# Revit family: Magnuson-Valuta-Planter+
name_source: partatom
category: Furniture
units: mm (PartAtom-declared; Revit-internal decimal feet)

## family parameters
Always vertical = Yes
Cut with Voids When Loaded = No
Room Calculation Point = No
Shared = No
Work Plane-Based = No

## types (4) — shared parameters
Assembly Code = E2020200
Base Finish = MAG - Anodized Silver
Body Finish = MAG - Anodized Silver
Default Elevation = 0"
Depth = 17 7/8"
Glide Finish = MAG - Plastic Black
Keynote = 12500
Liner Finish = MAG - Plastic Black
Manufacturer = Magnuson Group
Product Documentation Link = https://magnusongroup.com
Revit File Built By = https://servex-us.com
Soil Finish = MAG - soil
Top Finish = MAG - Anodized Silver
Type Comments = Planters
URL = www.magnusongroup.com
zero-valued in all types: Cost

## per-type parameters (varying)
| type | Description | Height | Liner Height | Opening Depth | Opening Width | Width |
| VA1809L-JR-P | Indoor junior height painted steel rectangular planter with internal rigid liner and adjustable glides. | 26 1/8" | 6" | 13 19/32" | 4 19/32" | 8 7/8" |
| VA1818L-P | Indoor painted steel square planter with internal rigid liner and adjustable glides. | 34 7/32" | 12" | 12" | 12" | 17 7/8" |
| VA1814L-P | Indoor painted steel rectangular planter with internal rigid liner and adjustable glides. | 34 7/32" | 8" | 12" | 8" | 13 7/8" |
| VA1809L-P | Indoor painted steel rectangular planter with internal rigid liner and adjustable glides. | 34 7/32" | 6" | 13 19/32" | 4 19/32" | 8 7/8" |

note: column(s) folded — value = type name in every type: Model

## geometry (parser evidence)
native form markers: Sweep x4
no freeform markers — native parametric forms only
